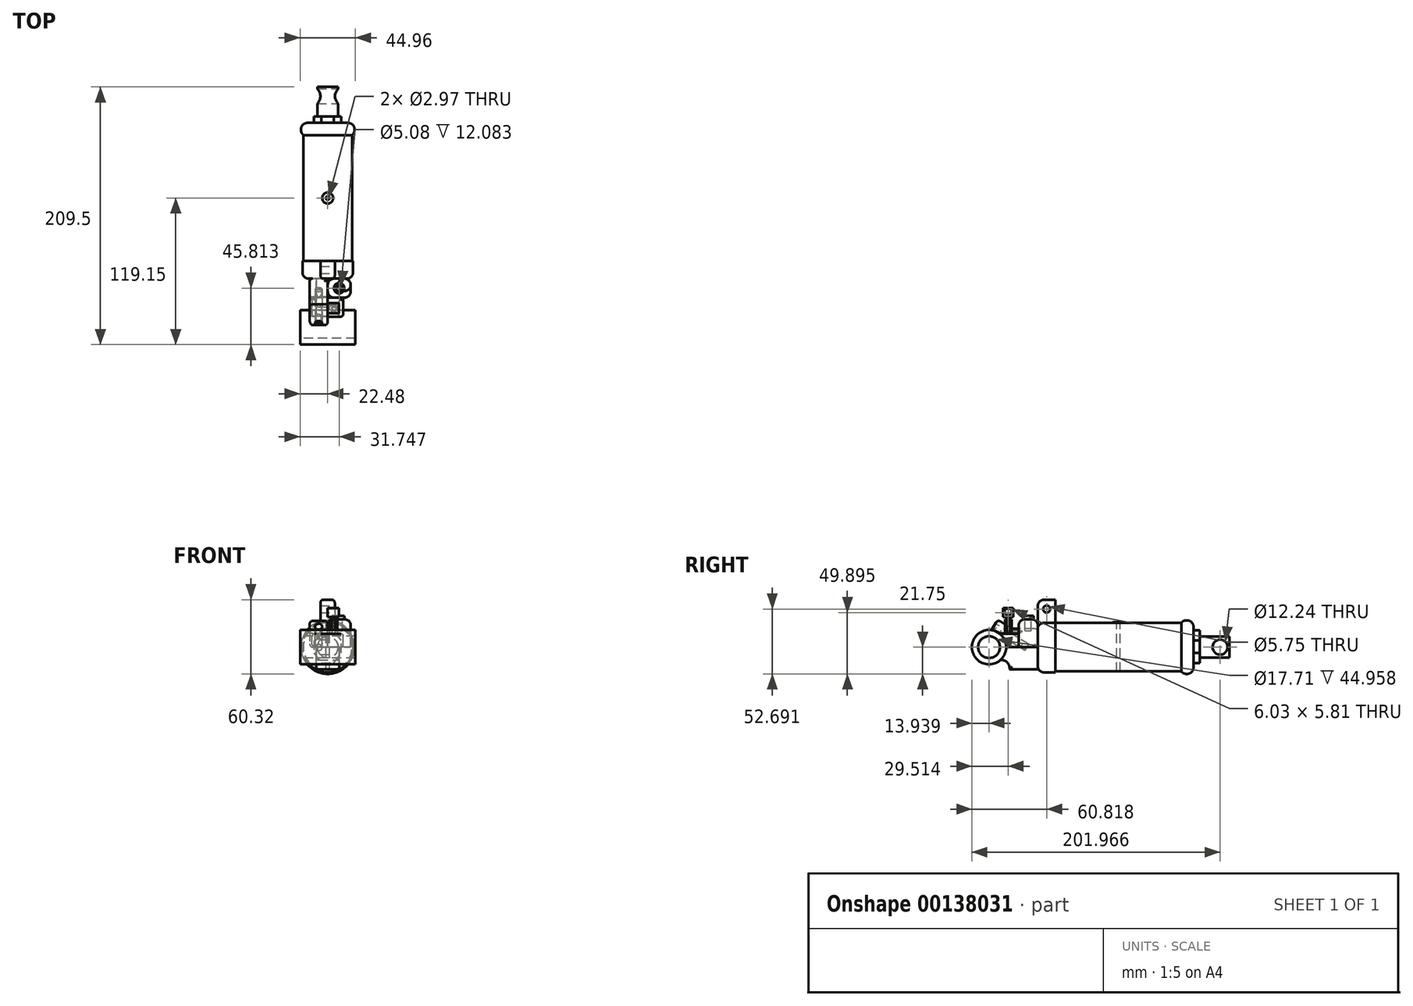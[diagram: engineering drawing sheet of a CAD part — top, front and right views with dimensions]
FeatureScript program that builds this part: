
annotation { "Feature Type Name" : "Feature", "Feature Type Description" : "" }
export const myFeature = defineFeature(function(context is Context, id is Id, definition is map)
    precondition{}
    {
        {
            var Q0;
            Q0=qCreatedBy(makeId("Front.planeOp"),FACE);
            var sketch = newSketch(context, id + "F0", { "sketchPlane" : qUnion([Q0])});
            skCircle(sketch, "E0", {"center": v(0, 0) * mm, "radius": 19.78 * mm});
            skSolve(sketch);
        }
        {
            var Q0;
            Q0 = qSketchRegion(id + "F0", true);
            extrude(context, id + "F1", {"entities" : qUnion([Q0]), "endBound" : BoundingType.SYMMETRIC, "depth" : 102.44 * mm});
        }
        {
            var Q0;
            Q0=makeQuery(id+"F1.opExtrude","CAP_FACE",FACE,{"disambiguationData":[OSD([sQuery(id+"F0.wireOp",EDGE,"E0")])],"isStart":true});
            var sketch = newSketch(context, id + "F2", { "sketchPlane" : qUnion([Q0])});
            skCircle(sketch, "E1", {"center": v(0, 0) * mm, "radius": 21.75 * mm});
            skSolve(sketch);
        }
        {
            var Q0;
            Q0 = qSketchRegion(id + "F2", true);
            extrude(context, id + "F3", {"entities" : qUnion([Q0]), "operationType" : NewBodyOperationType.ADD, "depth" : 9.88 * mm});
        }
        {
            var Q0;
            Q0=makeQuery(id+"F3.opExtrude","CAP_FACE",FACE,{"disambiguationData":[OSD([sQuery(id+"F2.wireOp",EDGE,"E1")])],"isStart":false});
            var sketch = newSketch(context, id + "F4", { "sketchPlane" : qUnion([Q0])});
            skLineSegment(sketch, "E2", {"start": v(-4.97, 13.58) * mm, "end": v(5.19, 13.58) * mm});
            skLineSegment(sketch, "E3", {"start": v(5.19, 13.58) * mm, "end": v(11.28, 5.45) * mm});
            skLineSegment(sketch, "E4", {"start": v(11.28, 5.45) * mm, "end": v(11.28, -4.7) * mm});
            skLineSegment(sketch, "E5", {"start": v(11.28, -4.7) * mm, "end": v(5.19, -12.84) * mm});
            skLineSegment(sketch, "E6", {"start": v(5.19, -12.84) * mm, "end": v(-4.97, -12.84) * mm});
            skLineSegment(sketch, "E7", {"start": v(-4.97, -12.84) * mm, "end": v(-11.07, -4.7) * mm});
            skLineSegment(sketch, "E8", {"start": v(-11.07, -4.7) * mm, "end": v(-11.07, 5.45) * mm});
            skLineSegment(sketch, "E9", {"start": v(-11.07, 5.45) * mm, "end": v(-4.97, 13.58) * mm});
            skSolve(sketch);
        }
        {
            var Q0;
            Q0 = qSketchRegion(id + "F4", true);
            extrude(context, id + "F5", {"entities" : qUnion([Q0]), "operationType" : NewBodyOperationType.ADD, "depth" : 5.07 * mm});
        }
        {
            var Q0;
            Q0=makeQuery(id+"F5.opExtrude","CAP_FACE",FACE,{"disambiguationData":[OSD([sQuery(id+"F4.wireOp",EDGE,"E2"),sQuery(id+"F4.wireOp",EDGE,"E3"),sQuery(id+"F4.wireOp",EDGE,"E4"),sQuery(id+"F4.wireOp",EDGE,"E5"),sQuery(id+"F4.wireOp",EDGE,"E6"),sQuery(id+"F4.wireOp",EDGE,"E7"),sQuery(id+"F4.wireOp",EDGE,"E8"),sQuery(id+"F4.wireOp",EDGE,"E9")])],"isStart":false});
            var sketch = newSketch(context, id + "F6", { "sketchPlane" : qUnion([Q0])});
            skCircle(sketch, "E10", {"center": v(0, 0) * mm, "radius": 8.5 * mm});
            skSolve(sketch);
        }
        {
            var Q0;
            Q0 = qSketchRegion(id + "F6", true);
            extrude(context, id + "F7", {"entities" : qUnion([Q0]), "operationType" : NewBodyOperationType.ADD, "depth" : 24.18 * mm});
        }
        {
            var Q0;
            Q0=qCreatedBy(makeId("Right.planeOp"),FACE);
            var sketch = newSketch(context, id + "F8", { "sketchPlane" : qUnion([Q0])});
            skCircle(sketch, "E11", {"center": v(82.82, 0) * mm, "radius": 6.12 * mm});
            skSolve(sketch);
        }
        {
            var Q0;
            Q0 = qSketchRegion(id + "F8", true);
            extrude(context, id + "F9", {"entities" : qUnion([Q0]), "operationType" : NewBodyOperationType.REMOVE, "endBound" : BoundingType.SYMMETRIC, "oppositeDirection" : true, "depth" : 25.4 * mm});
        }
        {
            var Q0;
            Q0=qCreatedBy(makeId("Top.planeOp"),FACE);
            cPlane(context, id + "F10", {"entities" : qUnion([Q0]), "cplaneType" : CPlaneType.OFFSET, "offset" : 19.78 * mm, "width" : 152.4 * mm, "height" : 152.4 * mm});
        }
        {
            var Q0;
            Q0=qCreatedBy(id+"F10.planeOp",FACE);
            var sketch = newSketch(context, id + "F11", { "sketchPlane" : qUnion([Q0])});
            skCircle(sketch, "E12", {"center": v(0, 0) * mm, "radius": 4.5 * mm});
            skSolve(sketch);
        }
        {
            var Q0;
            Q0 = qSketchRegion(id + "F11", true);
            extrude(context, id + "F12", {"entities" : qUnion([Q0]), "depth" : 0.62 * mm});
        }
        {
            var Q0;
            Q0=makeQuery(id+"F12.opExtrude","CAP_FACE",FACE,{"disambiguationData":[OSD([sQuery(id+"F11.wireOp",EDGE,"E12")])],"isStart":false});
            var sketch = newSketch(context, id + "F13", { "sketchPlane" : qUnion([Q0])});
            skCircle(sketch, "E13", {"center": v(0, 0) * mm, "radius": 1.48 * mm});
            skSolve(sketch);
        }
        {
            var Q0;
            Q0 = qSketchRegion(id + "F13", true);
            extrude(context, id + "F14", {"entities" : qUnion([Q0]), "operationType" : NewBodyOperationType.REMOVE, "oppositeDirection" : true, "depth" : 152.4 * mm});
        }
        {
            var Q0;
            Q0=makeQuery(id+"F1.opExtrude","CAP_FACE",FACE,{"disambiguationData":[OSD([sQuery(id+"F0.wireOp",EDGE,"E0")])],"isStart":false});
            var sketch = newSketch(context, id + "F15", { "sketchPlane" : qUnion([Q0])});
            skCircle(sketch, "E14", {"center": v(0, 0) * mm, "radius": 20.57 * mm});
            skLineSegment(sketch, "E15", {"start": v(-5.98, 19.68) * mm, "end": v(-5.98, 38.57) * mm});
            skLineSegment(sketch, "E16", {"start": v(-5.98, 38.57) * mm, "end": v(5.75, 38.57) * mm});
            skLineSegment(sketch, "E17", {"start": v(5.75, 38.57) * mm, "end": v(5.75, 19.75) * mm});
            skSolve(sketch);
        }
        {
            var Q0;
            Q0 = qSketchRegion(id + "F15", true);
            extrude(context, id + "F16", {"entities" : qUnion([Q0]), "operationType" : NewBodyOperationType.ADD, "depth" : 14.33 * mm});
        }
        {
            var Q0;
            Q0=makeQuery(id+"F16.opExtrude","CAP_EDGE",EDGE,{"disambiguationData":[OSD([sQuery(id+"F15.wireOp",EDGE,"E16")])],"isStart":false});
            fillet(context, id + "F17", {"entities" : qUnion([Q0]), "radius" : 5.08 * mm, "tangentPropagation" : true, "allowEdgeOverflow" : false});
        }
        {
            var Q0;
            Q0=makeQuery(id+"F16.opExtrude","SWEPT_EDGE",EDGE,{"disambiguationData":[OSD([sQuery(id+"F15.wireOp",EDGE,"E16"),sQuery(id+"F15.wireOp",EDGE,"E17")])]});
            var Q1;
            Q1=makeQuery(id+"F16.opExtrude","SWEPT_EDGE",EDGE,{"disambiguationData":[OSD([sQuery(id+"F15.wireOp",EDGE,"E15"),sQuery(id+"F15.wireOp",EDGE,"E16")])]});
            fillet(context, id + "F18", {"entities" : qUnion([Q0, Q1]), "radius" : 2.54 * mm, "tangentPropagation" : true, "allowEdgeOverflow" : false});
        }
        {
            var Q0;
            Q0=makeQuery(id+"F16.opExtrude","SWEPT_FACE",FACE,{"disambiguationData":[OSD([sQuery(id+"F15.wireOp",EDGE,"E17")])]});
            var sketch = newSketch(context, id + "F19", { "sketchPlane" : qUnion([Q0])});
            skCircle(sketch, "E18", {"center": v(-58.33, 30.94) * mm, "radius": 2.87 * mm});
            skSolve(sketch);
        }
        {
            var Q0;
            Q0 = qSketchRegion(id + "F19", true);
            extrude(context, id + "F20", {"entities" : qUnion([Q0]), "operationType" : NewBodyOperationType.REMOVE, "endBound" : BoundingType.THROUGH_ALL, "oppositeDirection" : true, "depth" : 25.4 * mm});
        }
        {
            var Q0;
            Q0=qCreatedBy(makeId("Right.planeOp"),FACE);
            var sketch = newSketch(context, id + "F21", { "sketchPlane" : qUnion([Q0])});
            skLineSegment(sketch, "E19", {"start": v(-65.55, -17.99) * mm, "end": v(-88.58, -17.99) * mm});
            skArc(sketch, "E20", {"start": v(-88.58, -17.99) * mm, "mid": v(-90.47, -12.4) * mm, "end": v(-96.05, -10.5) * mm});
            skCircle(sketch, "E21", {"center": v(-105.21, 0) * mm, "radius": 13.94 * mm});
            skCircle(sketch, "E22", {"center": v(-105.21, 0) * mm, "radius": 8.86 * mm});
            skLineSegment(sketch, "E23", {"start": v(-96.43, 10.84) * mm, "end": v(-81.06, 10.84) * mm});
            skLineSegment(sketch, "E24", {"start": v(-81.06, 0) * mm, "end": v(-81.06, 22.72) * mm});
            skLineSegment(sketch, "E25", {"start": v(-81.06, 22.72) * mm, "end": v(-65.54, 22.72) * mm});
            skLineSegment(sketch, "E26", {"start": v(-65.54, 22.72) * mm, "end": v(-65.55, -17.99) * mm});
            skLineSegment(sketch, "E27", {"start": v(-81.06, 0) * mm, "end": v(-65.54, 0) * mm});
            skLineSegment(sketch, "E28", {"start": v(-81.06, 0) * mm, "end": v(-91.27, 0) * mm});
            skSolve(sketch);
        }
        {
            var Q0;
            {var subQ1=sQuery(id+"F21.wireOp",EDGE,"E19");Q0=makeQuery(id+"F21.imprint","IMPRINT",FACE,{"disambiguationData":[TD([[makeQuery(id+"F21.imprint","IMPRINT",EDGE,{"derivedFrom":subQ1}),-1.0]])]});}
            extrude(context, id + "F22", {"entities" : qUnion([Q0]), "endBound" : BoundingType.SYMMETRIC, "oppositeDirection" : true, "depth" : 18.93 * mm});
        }
        {
            var Q0;
            {var subQ0=sQuery(id+"F21.wireOp",EDGE,"E25");Q0=makeQuery(id+"F21.imprint","IMPRINT",FACE,{"disambiguationData":[TD([[makeQuery(id+"F21.imprint","IMPRINT",EDGE,{"derivedFrom":subQ0}),-1.0]])]});}
            extrude(context, id + "F23", {"entities" : qUnion([Q0]), "depth" : 18.67 * mm});
        }
        {
            var Q0;
            {var subQ0=sQuery(id+"F21.wireOp",EDGE,"E23");Q0=makeQuery(id+"F21.imprint","IMPRINT",FACE,{"disambiguationData":[TD([[makeQuery(id+"F21.imprint","IMPRINT",EDGE,{"derivedFrom":subQ0}),-1.0]])]});}
            extrude(context, id + "F24", {"entities" : qUnion([Q0]), "endBound" : BoundingType.SYMMETRIC, "depth" : 25.4 * mm});
        }
        {
            var Q0;
            Q0=makeQuery(id+"F21.imprint","IMPRINT",FACE,{"disambiguationData":[TD([[makeQuery(id+"F21.imprint","IMPRINT",EDGE,{"derivedFrom":sQuery(id+"F21.wireOp",EDGE,"E22")}),-1.0]])]});
            extrude(context, id + "F25", {"entities" : qUnion([Q0]), "endBound" : BoundingType.SYMMETRIC, "depth" : 44.96 * mm});
        }
        {
            var Q0;
            Q0=makeQuery(id+"F23.opExtrude","CAP_EDGE",EDGE,{"disambiguationData":[OSD([sQuery(id+"F21.wireOp",EDGE,"E25")])],"isStart":false});
            var Q1;
            Q1=makeQuery(id+"F23.opExtrude","CAP_EDGE",EDGE,{"disambiguationData":[OSD([sQuery(id+"F21.wireOp",EDGE,"E24")])],"isStart":false});
            var Q2;
            Q2=makeQuery(id+"F23.opExtrude","CAP_EDGE",EDGE,{"disambiguationData":[OSD([sQuery(id+"F21.wireOp",EDGE,"E26")])],"isStart":false});
            var Q3;
            Q3=makeQuery(id+"F23.opExtrude","SWEPT_EDGE",EDGE,{"disambiguationData":[OSD([sQuery(id+"F21.wireOp",EDGE,"E25"),sQuery(id+"F21.wireOp",EDGE,"E26")])]});
            var Q4;
            Q4=makeQuery(id+"F23.opExtrude","CAP_EDGE",EDGE,{"disambiguationData":[OSD([sQuery(id+"F21.wireOp",EDGE,"E24")])],"isStart":true});
            var Q5;
            Q5=makeQuery(id+"F23.opExtrude","CAP_EDGE",EDGE,{"disambiguationData":[OSD([sQuery(id+"F21.wireOp",EDGE,"E25")])],"isStart":true});
            fillet(context, id + "F26", {"entities" : qUnion([Q0, Q1, Q2, Q3, Q4, Q5]), "radius" : 5.08 * mm, "tangentPropagation" : true, "allowEdgeOverflow" : false});
        }
        {
            var Q0;
            Q0=makeQuery(id+"F16.opExtrude","CAP_EDGE",EDGE,{"disambiguationData":[OSD([sQuery(id+"F15.wireOp",EDGE,"E14")])],"isStart":false});
            var Q1;
            {var subQ0=sQuery(id+"F21.wireOp",EDGE,"E26");var subQ1=sQuery(id+"F21.wireOp",EDGE,"E25");Q1=makeQuery(id+"F26.opFillet","BLEND_FACE",FACE,{"disambiguationData":[OSD([subQ1,subQ0]),TDD([makeQuery(id+"F23.opExtrude","SWEPT_EDGE",EDGE,{"disambiguationData":[OSD([subQ1,subQ0])]})])]});}
            var Q2;
            Q2=makeQuery(id+"F23.opExtrude","SWEPT_EDGE",EDGE,{"disambiguationData":[OSD([sQuery(id+"F21.wireOp",EDGE,"E24"),sQuery(id+"F21.wireOp",EDGE,"E25")])]});
            fillet(context, id + "F27", {"entities" : qUnion([Q0, Q1, Q2]), "radius" : 5.08 * mm, "tangentPropagation" : true, "allowEdgeOverflow" : false});
        }
        {
            var Q0;
            Q0=makeQuery(id+"F23.opExtrude","SWEPT_FACE",FACE,{"disambiguationData":[OSD([sQuery(id+"F21.wireOp",EDGE,"E25")])]});
            var sketch = newSketch(context, id + "F28", { "sketchPlane" : qUnion([Q0])});
            skPoint(sketch, "E29.centerSnap0", {"position": v(9.34, -75.98) * mm});
            skCircle(sketch, "E30", {"center": v(9.27, -73.34) * mm, "radius": 4.22 * mm});
            skSolve(sketch);
        }
        {
            var Q0;
            Q0 = qSketchRegion(id + "F28", true);
            extrude(context, id + "F29", {"entities" : qUnion([Q0]), "operationType" : NewBodyOperationType.ADD, "depth" : 2.35 * mm});
        }
        {
            var Q0;
            Q0 = qSketchRegion(id + "F28", true);
            extrude(context, id + "F30", {"entities" : qUnion([Q0]), "operationType" : NewBodyOperationType.ADD, "depth" : 2.86 * mm});
        }
        {
            var Q0;
            Q0=makeQuery(id+"F30.opExtrude","CAP_FACE",FACE,{"disambiguationData":[OSD([sQuery(id+"F28.wireOp",EDGE,"E30")])],"isStart":false});
            var sketch = newSketch(context, id + "F31", { "sketchPlane" : qUnion([Q0])});
            skCircle(sketch, "E31", {"center": v(9.27, -73.34) * mm, "radius": 2.54 * mm});
            skSolve(sketch);
        }
        {
            var Q0;
            Q0 = qSketchRegion(id + "F31", true);
            extrude(context, id + "F32", {"entities" : qUnion([Q0]), "operationType" : NewBodyOperationType.REMOVE, "oppositeDirection" : true, "depth" : 12.08 * mm});
        }
        {
            var Q0;
            Q0=makeQuery(id+"F24.opExtrude","CAP_EDGE",EDGE,{"disambiguationData":[OSD([sQuery(id+"F21.wireOp",EDGE,"E23")])],"isStart":false});
            var Q1;
            Q1=makeQuery(id+"F24.opExtrude","CAP_EDGE",EDGE,{"disambiguationData":[OSD([sQuery(id+"F21.wireOp",EDGE,"E23")])],"isStart":true});
            var Q2;
            Q2=makeQuery(id+"F24.opExtrude","SWEPT_EDGE",EDGE,{"disambiguationData":[OSD([sQuery(id+"F21.wireOp",EDGE,"E23"),sQuery(id+"F21.wireOp",EDGE,"E24")])]});
            var Q3;
            Q3=makeQuery(id+"F22.opExtrude","CAP_EDGE",EDGE,{"disambiguationData":[OSD([sQuery(id+"F21.wireOp",EDGE,"E27"),sQuery(id+"F21.wireOp",EDGE,"E28")])],"isStart":false});
            var Q4;
            Q4=makeQuery(id+"F22.opExtrude","CAP_EDGE",EDGE,{"disambiguationData":[OSD([sQuery(id+"F21.wireOp",EDGE,"E19")])],"isStart":true});
            var Q5;
            Q5=makeQuery(id+"F22.opExtrude","CAP_EDGE",EDGE,{"disambiguationData":[OSD([sQuery(id+"F21.wireOp",EDGE,"E20")])],"isStart":true});
            var Q6;
            Q6=makeQuery(id+"F24.opExtrude","CAP_EDGE",EDGE,{"disambiguationData":[OSD([sQuery(id+"F21.wireOp",EDGE,"E28")])],"isStart":false});
            fillet(context, id + "F33", {"entities" : qUnion([Q0, Q1, Q2, Q3, Q4, Q5, Q6]), "radius" : 2.03 * mm, "tangentPropagation" : true, "allowEdgeOverflow" : false});
        }
        {
            var Q0;
            Q0=makeQuery(id+"F22.opExtrude","CAP_EDGE",EDGE,{"disambiguationData":[OSD([sQuery(id+"F21.wireOp",EDGE,"E19")])],"isStart":false});
            var Q1;
            Q1=makeQuery(id+"F22.opExtrude","CAP_EDGE",EDGE,{"disambiguationData":[OSD([sQuery(id+"F21.wireOp",EDGE,"E20")])],"isStart":false});
            var Q2;
            Q2=makeQuery(id+"F24.opExtrude","CAP_EDGE",EDGE,{"disambiguationData":[OSD([sQuery(id+"F21.wireOp",EDGE,"E28")])],"isStart":true});
            fillet(context, id + "F34", {"entities" : qUnion([Q0, Q1, Q2]), "radius" : 2.03 * mm, "tangentPropagation" : true, "allowEdgeOverflow" : false});
        }
        {
            var Q0;
            {var subQ0=sQuery(id+"F21.wireOp",EDGE,"E25");Q0=makeQuery(id+"F21.imprint","IMPRINT",FACE,{"disambiguationData":[TD([[makeQuery(id+"F21.imprint","IMPRINT",EDGE,{"derivedFrom":subQ0}),-1.0]])]});}
            var sketch = newSketch(context, id + "F35", { "sketchPlane" : qUnion([Q0])});
            skLineSegment(sketch, "E32", {"start": v(-65.36, 14.9) * mm, "end": v(-86.46, 14.9) * mm});
            skLineSegment(sketch, "E33", {"start": v(-86.46, 14.9) * mm, "end": v(-98.1, 22.23) * mm});
            skLineSegment(sketch, "E34", {"start": v(-98.1, 22.23) * mm, "end": v(-103.37, 13.85) * mm});
            skArc(sketch, "E35", {"start": v(-91.2, 0) * mm, "mid": v(-94.44, 9.43) * mm, "end": v(-103.37, 13.85) * mm});
            skLineSegment(sketch, "E36", {"start": v(-65.36, 14.9) * mm, "end": v(-65.36, 0) * mm});
            skLineSegment(sketch, "E37", {"start": v(-65.36, 0) * mm, "end": v(-80.43, 0) * mm});
            skLineSegment(sketch, "E38", {"start": v(-80.43, 0) * mm, "end": v(-80.43, 11.03) * mm});
            skLineSegment(sketch, "E39", {"start": v(-80.43, 11.03) * mm, "end": v(-96.13, 11.03) * mm});
            skSolve(sketch);
        }
        {
            var Q0;
            Q0 = qSketchRegion(id + "F35", true);
            extrude(context, id + "F36", {"entities" : qUnion([Q0]), "oppositeDirection" : true, "depth" : 14.7 * mm});
        }
        {
            var Q0;
            Q0=makeQuery(id+"F36.opExtrude","CAP_EDGE",EDGE,{"disambiguationData":[OSD([sQuery(id+"F35.wireOp",EDGE,"E37")])],"isStart":false});
            var Q1;
            Q1=makeQuery(id+"F36.opExtrude","CAP_EDGE",EDGE,{"disambiguationData":[OSD([sQuery(id+"F35.wireOp",EDGE,"E38")])],"isStart":false});
            var Q2;
            Q2=makeQuery(id+"F36.opExtrude","CAP_EDGE",EDGE,{"disambiguationData":[OSD([sQuery(id+"F35.wireOp",EDGE,"E39")])],"isStart":false});
            var Q3;
            Q3=makeQuery(id+"F36.opExtrude","CAP_EDGE",EDGE,{"disambiguationData":[OSD([sQuery(id+"F35.wireOp",EDGE,"E35")])],"isStart":false});
            var Q4;
            Q4=makeQuery(id+"F36.opExtrude","CAP_EDGE",EDGE,{"disambiguationData":[OSD([sQuery(id+"F35.wireOp",EDGE,"E34")])],"isStart":false});
            var Q5;
            Q5=makeQuery(id+"F36.opExtrude","CAP_EDGE",EDGE,{"disambiguationData":[OSD([sQuery(id+"F35.wireOp",EDGE,"E33")])],"isStart":false});
            var Q6;
            Q6=makeQuery(id+"F36.opExtrude","SWEPT_EDGE",EDGE,{"disambiguationData":[OSD([sQuery(id+"F35.wireOp",EDGE,"E33"),sQuery(id+"F35.wireOp",EDGE,"E34")])]});
            var Q7;
            Q7=makeQuery(id+"F36.opExtrude","CAP_EDGE",EDGE,{"disambiguationData":[OSD([sQuery(id+"F35.wireOp",EDGE,"E32")])],"isStart":false});
            var Q8;
            Q8=makeQuery(id+"F36.opExtrude","CAP_EDGE",EDGE,{"disambiguationData":[OSD([sQuery(id+"F35.wireOp",EDGE,"E32")])],"isStart":true});
            var Q9;
            Q9=makeQuery(id+"F36.opExtrude","SWEPT_EDGE",EDGE,{"disambiguationData":[OSD([sQuery(id+"F35.wireOp",EDGE,"E32"),sQuery(id+"F35.wireOp",EDGE,"E36")])]});
            var Q10;
            Q10=makeQuery(id+"F36.opExtrude","CAP_EDGE",EDGE,{"disambiguationData":[OSD([sQuery(id+"F35.wireOp",EDGE,"E36")])],"isStart":false});
            var Q11;
            Q11=makeQuery(id+"F36.opExtrude","CAP_EDGE",EDGE,{"disambiguationData":[OSD([sQuery(id+"F35.wireOp",EDGE,"E34")])],"isStart":true});
            var Q12;
            Q12=makeQuery(id+"F36.opExtrude","CAP_EDGE",EDGE,{"disambiguationData":[OSD([sQuery(id+"F35.wireOp",EDGE,"E33")])],"isStart":true});
            fillet(context, id + "F37", {"entities" : qUnion([Q0, Q1, Q2, Q3, Q4, Q5, Q6, Q7, Q8, Q9, Q10, Q11, Q12]), "radius" : 2.54 * mm, "tangentPropagation" : true, "allowEdgeOverflow" : false});
        }
        {
            var Q0;
            Q0=makeQuery(id+"F36.opExtrude","SWEPT_FACE",FACE,{"disambiguationData":[OSD([sQuery(id+"F35.wireOp",EDGE,"E34")])]});
            var sketch = newSketch(context, id + "F38", { "sketchPlane" : qUnion([Q0])});
            skCircle(sketch, "E40", {"center": v(-7.46, -39.97) * mm, "radius": 2.94 * mm});
            skSolve(sketch);
        }
        {
            var Q0;
            Q0 = qSketchRegion(id + "F38", true);
            extrude(context, id + "F39", {"entities" : qUnion([Q0]), "operationType" : NewBodyOperationType.REMOVE, "oppositeDirection" : true, "depth" : 31.94 * mm});
        }
        {
            var Q0;
            Q0=makeQuery(id+"F24.opExtrude","SWEPT_FACE",FACE,{"disambiguationData":[OSD([sQuery(id+"F21.wireOp",EDGE,"E23")])]});
            var sketch = newSketch(context, id + "F40", { "sketchPlane" : qUnion([Q0])});
            skLineSegment(sketch, "E41", {"start": v(1.56, -90.61) * mm, "end": v(1.56, -88.2) * mm});
            skLineSegment(sketch, "E42", {"start": v(1.56, -88.2) * mm, "end": v(3.5, -86.74) * mm});
            skLineSegment(sketch, "E43", {"start": v(3.5, -86.74) * mm, "end": v(5.91, -86.74) * mm});
            skLineSegment(sketch, "E44", {"start": v(5.91, -86.74) * mm, "end": v(7.85, -88.2) * mm});
            skLineSegment(sketch, "E45", {"start": v(7.85, -88.2) * mm, "end": v(7.85, -90.61) * mm});
            skLineSegment(sketch, "E46", {"start": v(7.85, -90.61) * mm, "end": v(5.91, -92.06) * mm});
            skLineSegment(sketch, "E47", {"start": v(5.91, -92.06) * mm, "end": v(3.5, -92.06) * mm});
            skLineSegment(sketch, "E48", {"start": v(3.5, -92.06) * mm, "end": v(1.56, -90.61) * mm});
            skSolve(sketch);
        }
        {
            var Q0;
            Q0 = qSketchRegion(id + "F40", true);
            extrude(context, id + "F41", {"entities" : qUnion([Q0]), "operationType" : NewBodyOperationType.ADD, "depth" : 11.9 * mm});
        }
        {
            var Q0;
            Q0=makeQuery(id+"F41.opExtrude","CAP_FACE",FACE,{"disambiguationData":[OSD([sQuery(id+"F40.wireOp",EDGE,"E41"),sQuery(id+"F40.wireOp",EDGE,"E42"),sQuery(id+"F40.wireOp",EDGE,"E43"),sQuery(id+"F40.wireOp",EDGE,"E44"),sQuery(id+"F40.wireOp",EDGE,"E45"),sQuery(id+"F40.wireOp",EDGE,"E46"),sQuery(id+"F40.wireOp",EDGE,"E47"),sQuery(id+"F40.wireOp",EDGE,"E48")])],"isStart":false});
            var sketch = newSketch(context, id + "F42", { "sketchPlane" : qUnion([Q0])});
            skCircle(sketch, "E49", {"center": v(4.6, -89.64) * mm, "radius": 1.5 * mm});
            skSolve(sketch);
        }
        {
            var Q0;
            Q0=makeQuery(id+"F42.imprint","IMPRINT",FACE,{"disambiguationData":[TD([[makeQuery(id+"F42.imprint","IMPRINT",EDGE,{"derivedFrom":sQuery(id+"F42.wireOp",EDGE,"E49")}),1.0]])]});
            extrude(context, id + "F43", {"entities" : qUnion([Q0]), "operationType" : NewBodyOperationType.ADD, "depth" : 1.68 * mm});
        }
        {
            var Q0;
            Q0=makeQuery(id+"F43.opExtrude","CAP_FACE",FACE,{"disambiguationData":[OSD([sQuery(id+"F42.wireOp",EDGE,"E49")])],"isStart":false});
            var sketch = newSketch(context, id + "F44", { "sketchPlane" : qUnion([Q0])});
            skLineSegment(sketch, "E50.bottom", {"start": v(9.2, -85.54) * mm, "end": v(0, -85.54) * mm});
            skLineSegment(sketch, "E50.top", {"start": v(9.2, -93.73) * mm, "end": v(0, -93.73) * mm});
            skLineSegment(sketch, "E50.left", {"start": v(9.2, -85.54) * mm, "end": v(9.2, -93.73) * mm});
            skLineSegment(sketch, "E50.right", {"start": v(0, -85.54) * mm, "end": v(0, -93.73) * mm});
            skPoint(sketch, "E50.middle", {"position": v(4.6, -89.64) * mm});
            skSolve(sketch);
        }
        {
            var Q0;
            Q0 = qSketchRegion(id + "F44", true);
            extrude(context, id + "F45", {"entities" : qUnion([Q0]), "operationType" : NewBodyOperationType.ADD, "depth" : 7.47 * mm});
        }
        {
            var Q0;
            Q0=makeQuery(id+"F45.opExtrude","SWEPT_FACE",FACE,{"disambiguationData":[OSD([sQuery(id+"F44.wireOp",EDGE,"E50.left")])]});
            var sketch = newSketch(context, id + "F46", { "sketchPlane" : qUnion([Q0])});
            skLineSegment(sketch, "E51", {"start": v(-92.65, 31.05) * mm, "end": v(-92.65, 25.24) * mm});
            skLineSegment(sketch, "E52", {"start": v(-92.65, 25.24) * mm, "end": v(-86.62, 25.24) * mm});
            skLineSegment(sketch, "E53", {"start": v(-86.62, 25.24) * mm, "end": v(-86.62, 31.05) * mm});
            skLineSegment(sketch, "E54", {"start": v(-86.62, 31.05) * mm, "end": v(-92.65, 31.05) * mm});
            skSolve(sketch);
        }
        {
            var Q0;
            Q0 = qSketchRegion(id + "F46", true);
            extrude(context, id + "F47", {"entities" : qUnion([Q0]), "operationType" : NewBodyOperationType.REMOVE, "endBound" : BoundingType.THROUGH_ALL, "oppositeDirection" : true, "depth" : 25.4 * mm});
        }
        {
            var Q0;
            Q0=makeQuery(id+"F47.boolean.opBoolean","COPY",FACE,{"derivedFrom":makeQuery(id+"F47.opExtrude","SWEPT_FACE",FACE,{"disambiguationData":[OSD([sQuery(id+"F46.wireOp",EDGE,"E52")])]})});
            var sketch = newSketch(context, id + "F48", { "sketchPlane" : qUnion([Q0])});
            skCircle(sketch, "E55", {"center": v(5.3, -89.74) * mm, "radius": 1.78 * mm});
            skSolve(sketch);
        }
        {
            var Q0;
            Q0 = qSketchRegion(id + "F48", true);
            extrude(context, id + "F49", {"entities" : qUnion([Q0]), "operationType" : NewBodyOperationType.ADD, "depth" : 0.82 * mm});
        }
        {
            var Q0;
            Q0=makeQuery(id+"F3.opExtrude","CAP_EDGE",EDGE,{"disambiguationData":[OSD([sQuery(id+"F2.wireOp",EDGE,"E1")])],"isStart":true});
            var Q1;
            Q1=makeQuery(id+"F3.opExtrude","CAP_EDGE",EDGE,{"disambiguationData":[OSD([sQuery(id+"F2.wireOp",EDGE,"E1")])],"isStart":false});
            fillet(context, id + "F50", {"entities" : qUnion([Q0, Q1]), "radius" : 5.08 * mm, "tangentPropagation" : true, "allowEdgeOverflow" : false});
        }
    });
